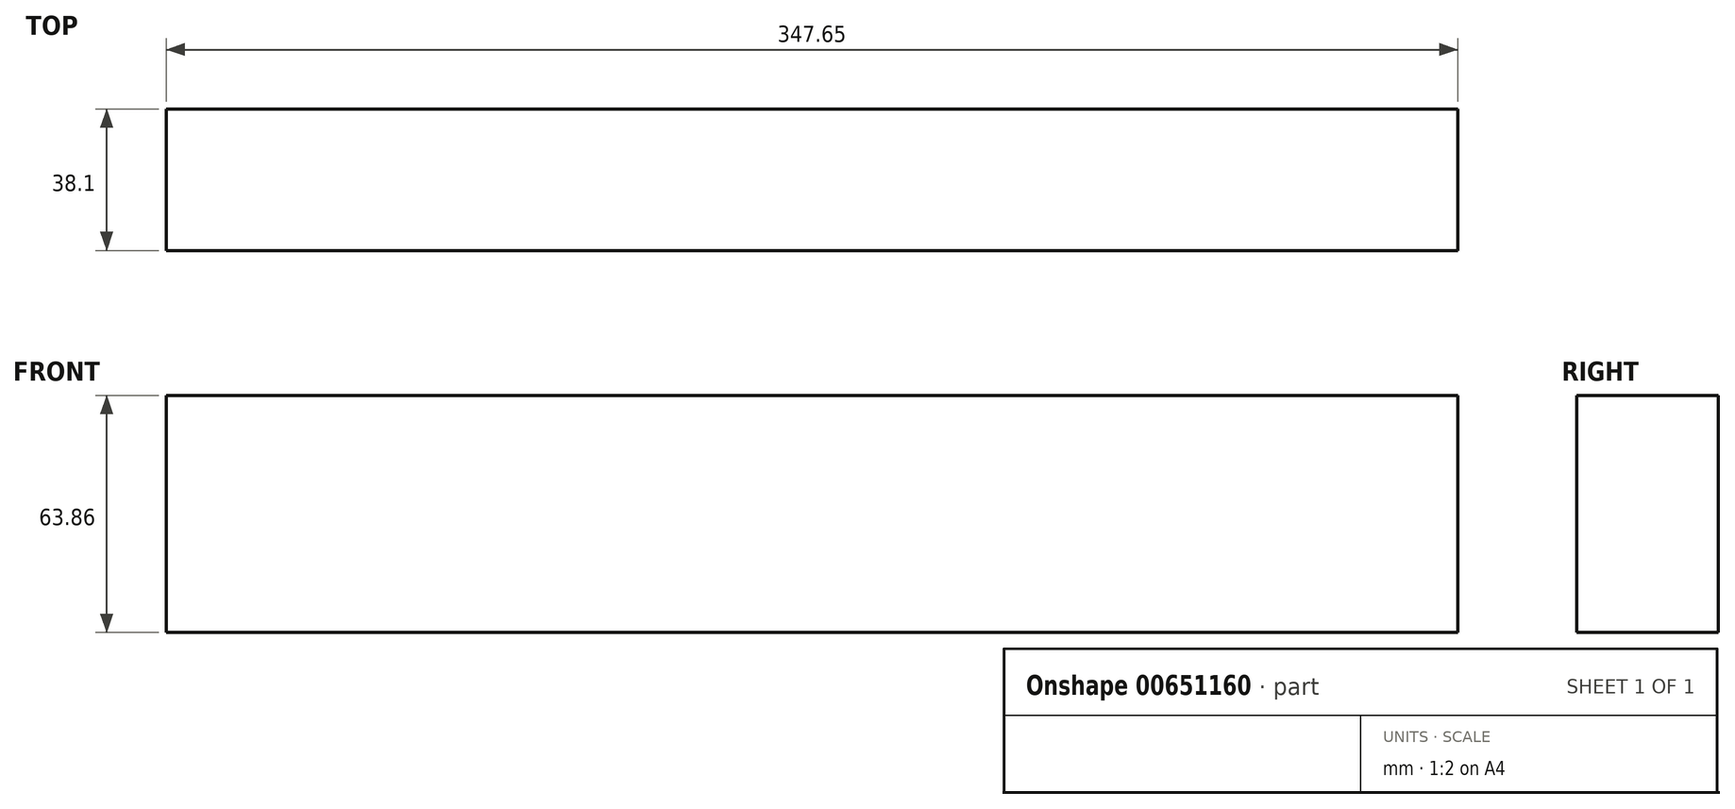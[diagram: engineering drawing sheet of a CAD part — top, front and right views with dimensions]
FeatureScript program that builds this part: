
annotation { "Feature Type Name" : "Feature", "Feature Type Description" : "" }
export const myFeature = defineFeature(function(context is Context, id is Id, definition is map)
    precondition{}
    {
        {
            var Q0;
            Q0=qCreatedBy(makeId("Right.planeOp"),FACE);
            var sketch = newSketch(context, id + "F0", { "sketchPlane" : qUnion([Q0])});
            skLineSegment(sketch, "E0.bottom", {"start": v(19.05, 31.93) * mm, "end": v(-19.05, 31.93) * mm});
            skLineSegment(sketch, "E0.top", {"start": v(19.05, -31.93) * mm, "end": v(-19.05, -31.93) * mm});
            skLineSegment(sketch, "E0.left", {"start": v(19.05, 31.93) * mm, "end": v(19.05, -31.93) * mm});
            skLineSegment(sketch, "E0.right", {"start": v(-19.05, 31.93) * mm, "end": v(-19.05, -31.93) * mm});
            skPoint(sketch, "E0.middle", {"position": v(0, 0) * mm});
            skSolve(sketch);
        }
        {
            var Q0;
            Q0=makeQuery(id+"F0.imprint","IMPRINT",FACE,{"disambiguationData":[TD([[makeQuery(id+"F0.imprint","IMPRINT",EDGE,{"derivedFrom":sQuery(id+"F0.wireOp",EDGE,"E0.bottom")}),1.0]])]});
            extrude(context, id + "F1", {"entities" : qUnion([Q0]), "depth" : 347.65 * mm, "offsetDistance" : 25.4 * mm});
        }
    });
